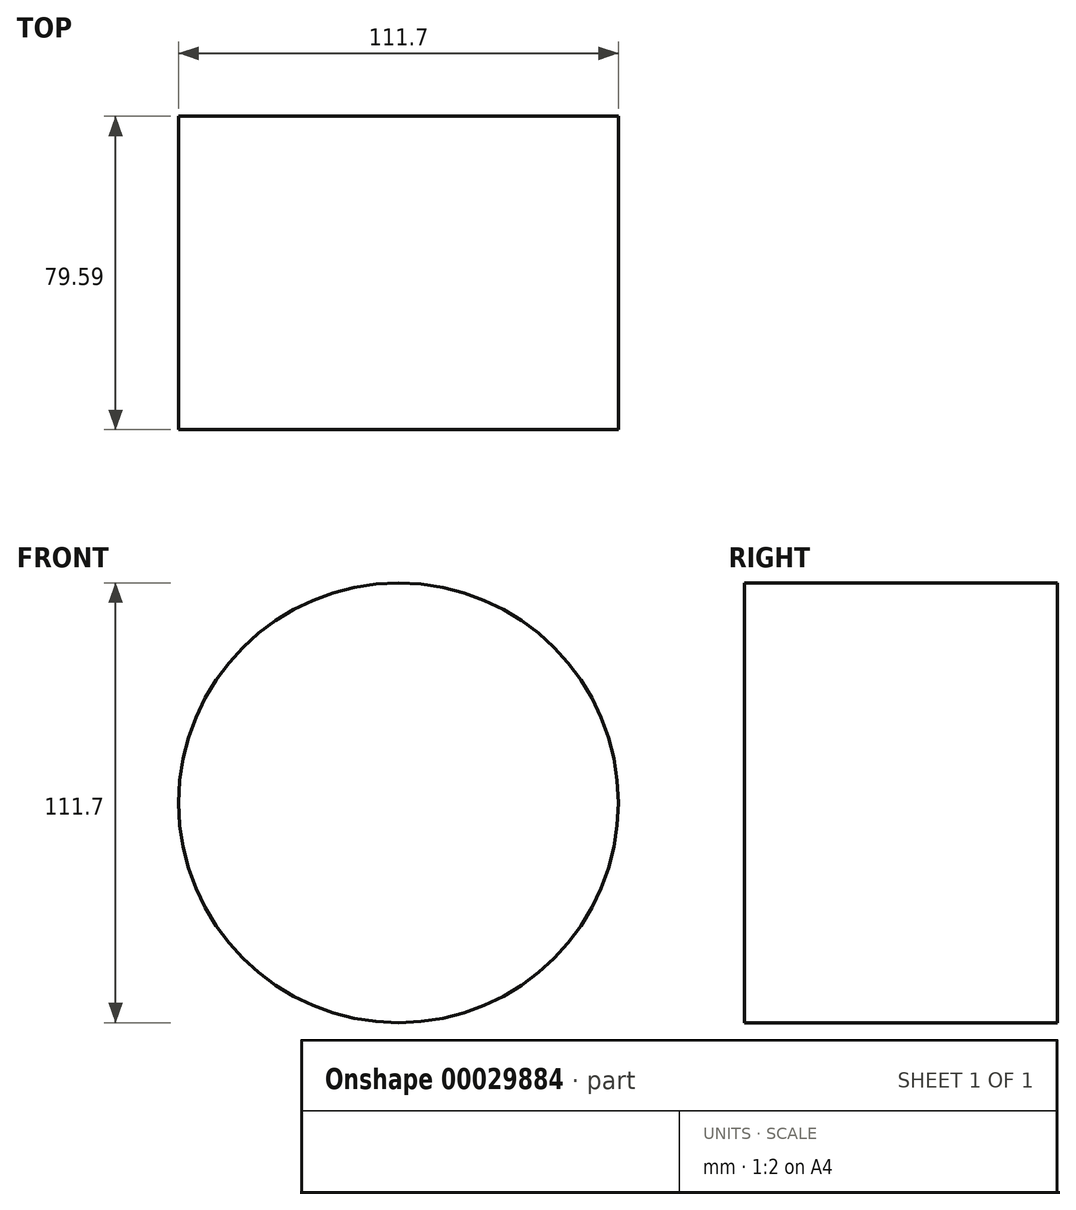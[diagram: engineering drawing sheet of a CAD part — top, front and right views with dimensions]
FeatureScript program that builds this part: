
annotation { "Feature Type Name" : "Feature", "Feature Type Description" : "" }
export const myFeature = defineFeature(function(context is Context, id is Id, definition is map)
    precondition{}
    {
        {
            var Q0;
            Q0=qCreatedBy(makeId("Front.planeOp"),FACE);
            var sketch = newSketch(context, id + "F0", { "sketchPlane" : qUnion([Q0])});
            skCircle(sketch, "E0", {"center": v(0, 0) * mm, "radius": 55.85 * mm});
            skSolve(sketch);
        }
        {
            var Q0;
            Q0 = qSketchRegion(id + "F0", true);
            extrude(context, id + "F1", {"entities" : qUnion([Q0]), "depth" : 79.6 * mm});
        }
        {
            var Q0;
            Q0=makeQuery(id+"F1.opExtrude","SWEPT_BODY",BODY,{"disambiguationData":[OSD([sQuery(id+"F0.wireOp",EDGE,"E0")])]});
            var Q1;
            Q1=makeQuery(id+"F1.opExtrude","CAP_EDGE",EDGE,{"disambiguationData":[OSD([sQuery(id+"F0.wireOp",EDGE,"E0")])],"isStart":false});
            circularPattern(context, id + "F2", {"entities" : qUnion([Q0]), "axis" : qUnion([Q1]), "angle" : 30 * degree, "instanceCount" : 5});
        }
        {
            var Q0;
            Q0=makeQuery(id+"F2.opPattern","COPY",BODY,{"derivedFrom":makeQuery(id+"F1.opExtrude","SWEPT_BODY",BODY,{"disambiguationData":[OSD([sQuery(id+"F0.wireOp",EDGE,"E0")])]}),"instanceName":"1"});
            transform(context, id + "F3", {"entities" : qUnion([Q0]), "transformType" : TransformType.COPY});
        }
    });
